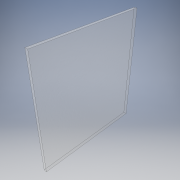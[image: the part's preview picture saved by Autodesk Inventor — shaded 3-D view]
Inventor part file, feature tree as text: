
AUTODESK INVENTOR PART (.ipt)
format: ipt  version: 2019 (Build 230136000, 136)  size: 100,352 bytes
history: native  units: in
note: dims shown in document units (in); Inventor stores cm internally (conversion verified against a paired STEP export)
features: extrude x1, sketch x1
ambient origin geometry x8: Origin, YZ Plane, XZ Plane, XY Plane, X Axis, Y Axis, Z Axis, Center Point
bodies: Solid1 (feature_tree)
feature tree (2):
  extrude  "Extrusion1"  Depth=7.5in
  sketch  "Sketch1"  dims[d0=8.0in d1=7.5in d2=0.21in d3=0.0in]
